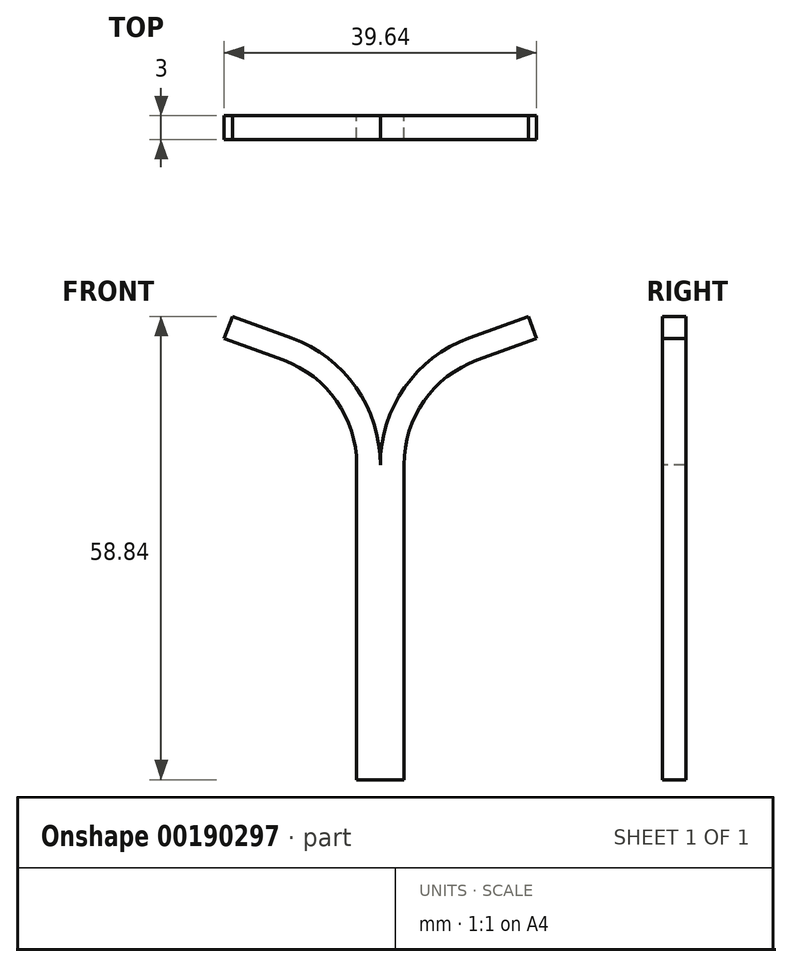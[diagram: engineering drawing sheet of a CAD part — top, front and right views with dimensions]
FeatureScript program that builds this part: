
annotation { "Feature Type Name" : "Feature", "Feature Type Description" : "" }
export const myFeature = defineFeature(function(context is Context, id is Id, definition is map)
    precondition{}
    {
        {
            var Q0;
            Q0=qCreatedBy(makeId("Front.planeOp"),FACE);
            var sketch = newSketch(context, id + "F0", { "sketchPlane" : qUnion([Q0])});
            skLineSegment(sketch, "E0", {"start": v(0, 0) * mm, "end": v(0, 40) * mm});
            skLineSegment(sketch, "E1", {"start": v(11.28, 56.1) * mm, "end": v(18.8, 58.84) * mm});
            skArc(sketch, "E2", {"start": v(11.28, 56.1) * mm, "mid": v(3.1, 49.83) * mm, "end": v(0, 40) * mm});
            skSolve(sketch);
        }
        {
            var Q0;
            Q0=qCreatedBy(makeId("Top.planeOp"),FACE);
            var sketch = newSketch(context, id + "F1", { "sketchPlane" : qUnion([Q0])});
            skLineSegment(sketch, "E3", {"start": v(0, 0) * mm, "end": v(3, 0) * mm, "construction": true});
            skLineSegment(sketch, "E4.0", {"start": v(0, -1.5) * mm, "end": v(3, -1.5) * mm});
            skLineSegment(sketch, "E5.MirrorCS", {"start": v(0, 1.5) * mm, "end": v(3, 1.5) * mm});
            skLineSegment(sketch, "E6", {"start": v(3, -1.5) * mm, "end": v(3, 1.5) * mm});
            skLineSegment(sketch, "E7", {"start": v(0, 1.5) * mm, "end": v(0, -1.5) * mm});
            skSolve(sketch);
        }
        {
            var Q0;
            Q0=makeQuery(id+"F1.imprint","IMPRINT",FACE,{"disambiguationData":[TD([[makeQuery(id+"F1.imprint","IMPRINT",EDGE,{"derivedFrom":sQuery(id+"F1.wireOp",EDGE,"E4.0")}),1.0]])]});
            var Q1;
            Q1=sQuery(id+"F0.wireOp",EDGE,"E0");
            var Q2;
            Q2=sQuery(id+"F0.wireOp",EDGE,"E2");
            var Q3;
            Q3=sQuery(id+"F0.wireOp",EDGE,"E1");
            sweep(context, id + "F2", {"profiles" : qUnion([Q0]), "path" : qUnion([Q1, Q2, Q3])});
        }
        {
            var Q0;
            Q0=makeQuery(id+"F2.opSweep","SWEPT_BODY",BODY,{"disambiguationData":[OSD([sQuery(id+"F0.wireOp",EDGE,"E1"),sQuery(id+"F1.wireOp",EDGE,"E4.0"),sQuery(id+"F1.wireOp",EDGE,"E5.MirrorCS"),sQuery(id+"F1.wireOp",EDGE,"E6"),sQuery(id+"F1.wireOp",EDGE,"E7")])]});
            var Q1;
            Q1=makeQuery(id+"F2.opSweep","SWEPT_FACE",FACE,{"disambiguationData":[OSD([sQuery(id+"F0.wireOp",EDGE,"E0"),sQuery(id+"F1.wireOp",EDGE,"E7")])]});
            mirror(context, id + "F3", {"operationType" : NewBodyOperationType.ADD, "entities" : qUnion([Q0]), "mirrorPlane" : qUnion([Q1])});
        }
    });
